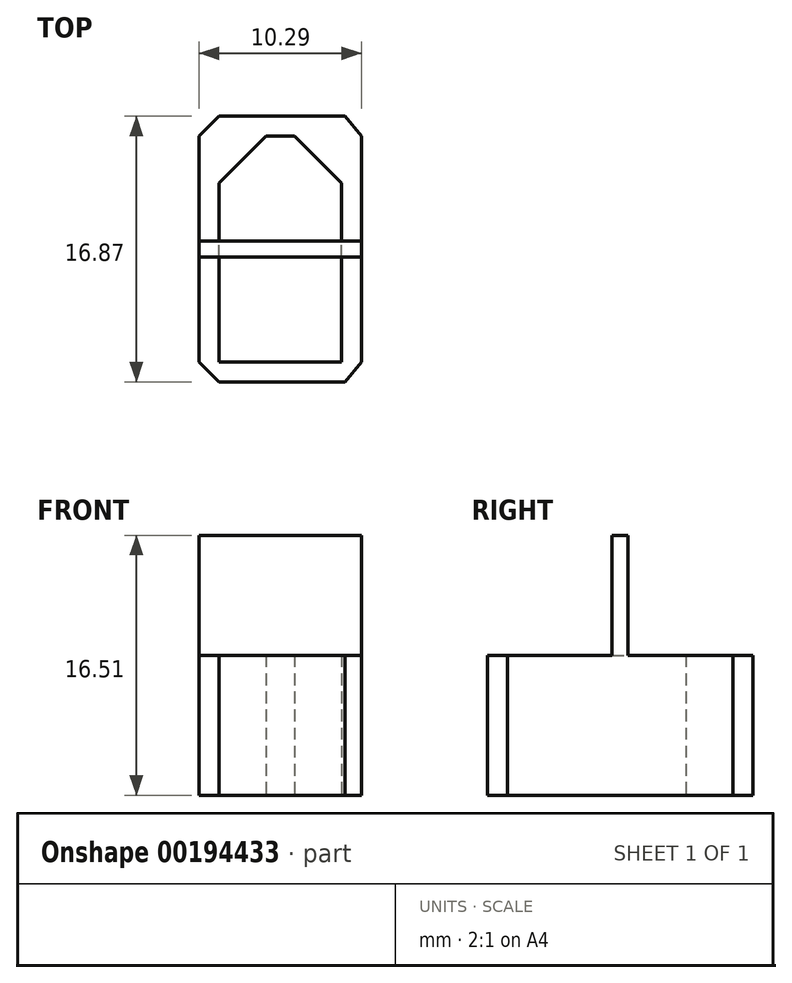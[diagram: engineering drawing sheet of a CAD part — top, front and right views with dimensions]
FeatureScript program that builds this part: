
annotation { "Feature Type Name" : "Feature", "Feature Type Description" : "" }
export const myFeature = defineFeature(function(context is Context, id is Id, definition is map)
    precondition{}
    {
        {
            var Q0;
            Q0=qCreatedBy(makeId("Top.planeOp"),FACE);
            var sketch = newSketch(context, id + "F0", { "sketchPlane" : qUnion([Q0])});
            skLineSegment(sketch, "E0.bottom", {"start": v(0, 0) * mm, "end": v(7.75, 0) * mm});
            skLineSegment(sketch, "E0.top", {"start": v(2.97, 14.33) * mm, "end": v(4.77, 14.33) * mm});
            skLineSegment(sketch, "E0.left", {"start": v(0, 0) * mm, "end": v(0, 11.35) * mm});
            skLineSegment(sketch, "E0.right", {"start": v(7.75, 0) * mm, "end": v(7.75, 11.35) * mm});
            skLineSegment(sketch, "E1", {"start": v(4.77, 14.33) * mm, "end": v(7.75, 11.35) * mm});
            skLineSegment(sketch, "E2", {"start": v(2.97, 14.33) * mm, "end": v(0, 11.35) * mm});
            skLineSegment(sketch, "E3.0", {"start": v(9.02, 0) * mm, "end": v(9.02, 14.33) * mm});
            skLineSegment(sketch, "E4.0", {"start": v(0, 15.6) * mm, "end": v(7.98, 15.6) * mm});
            skLineSegment(sketch, "E5.0", {"start": v(-1.27, 0) * mm, "end": v(-1.27, 14.33) * mm});
            skLineSegment(sketch, "E6.0", {"start": v(0, -1.27) * mm, "end": v(7.98, -1.27) * mm});
            skLineSegment(sketch, "E7", {"start": v(0, 15.6) * mm, "end": v(-1.27, 14.33) * mm});
            skLineSegment(sketch, "E8", {"start": v(7.98, 15.6) * mm, "end": v(9.02, 14.33) * mm});
            skLineSegment(sketch, "E9", {"start": v(9.02, 0) * mm, "end": v(7.98, -1.27) * mm});
            skLineSegment(sketch, "E10", {"start": v(0, -1.27) * mm, "end": v(-1.27, 0) * mm});
            skSolve(sketch);
        }
        {
            var Q0;
            Q0=makeQuery(id+"F0.imprint","IMPRINT",FACE,{"disambiguationData":[TD([[makeQuery(id+"F0.imprint","IMPRINT",EDGE,{"derivedFrom":sQuery(id+"F0.wireOp",EDGE,"E0.bottom")}),-1.0]])]});
            extrude(context, id + "F1", {"entities" : qUnion([Q0]), "depth" : 8.9 * mm});
        }
        {
            var Q0;
            Q0=makeQuery(id+"F1.opExtrude","CAP_FACE",FACE,{"disambiguationData":[OSD([sQuery(id+"F0.wireOp",EDGE,"E0.bottom"),sQuery(id+"F0.wireOp",EDGE,"E0.top"),sQuery(id+"F0.wireOp",EDGE,"E0.left"),sQuery(id+"F0.wireOp",EDGE,"E0.right"),sQuery(id+"F0.wireOp",EDGE,"E1"),sQuery(id+"F0.wireOp",EDGE,"E2"),sQuery(id+"F0.wireOp",EDGE,"E3.0"),sQuery(id+"F0.wireOp",EDGE,"E4.0"),sQuery(id+"F0.wireOp",EDGE,"E5.0"),sQuery(id+"F0.wireOp",EDGE,"E6.0"),sQuery(id+"F0.wireOp",EDGE,"E7"),sQuery(id+"F0.wireOp",EDGE,"E8"),sQuery(id+"F0.wireOp",EDGE,"E9"),sQuery(id+"F0.wireOp",EDGE,"E10")])],"isStart":false});
            var sketch = newSketch(context, id + "F2", { "sketchPlane" : qUnion([Q0])});
            skLineSegment(sketch, "E11.bottom", {"start": v(-1.27, 7.67) * mm, "end": v(9.02, 7.67) * mm});
            skLineSegment(sketch, "E11.top", {"start": v(-1.27, 6.65) * mm, "end": v(9.02, 6.65) * mm});
            skLineSegment(sketch, "E11.left", {"start": v(-1.27, 7.67) * mm, "end": v(-1.27, 6.65) * mm});
            skLineSegment(sketch, "E11.right", {"start": v(9.02, 7.67) * mm, "end": v(9.02, 6.65) * mm});
            skSolve(sketch);
        }
        {
            var Q0;
            {var subQ0=sQuery(id+"F2.wireOp",EDGE,"E11.right");Q0=makeQuery(id+"F2.imprint","IMPRINT",FACE,{"disambiguationData":[TD([[makeQuery(id+"F2.imprint","IMPRINT",EDGE,{"derivedFrom":subQ0}),1.0]])]});}
            var Q1;
            {var subQ0=sQuery(id+"F2.wireOp",EDGE,"E11.bottom");var subQ1=makeQuery(id+"F1.opExtrude","CAP_EDGE",EDGE,{"disambiguationData":[OSD([sQuery(id+"F0.wireOp",EDGE,"E0.left")])],"isStart":false});var subQ2=makeQuery(id+"F2.imprint","INTERSECT",VERTEX,{"derivedFrom":[subQ1,subQ0]});Q1=makeQuery(id+"F2.imprint","IMPRINT",FACE,{"disambiguationData":[TD([[makeQuery(id+"F2.imprint","IMPRINT",EDGE,{"disambiguationData":[TD([[subQ2,-1.0]])],"derivedFrom":subQ0}),-1.0]])]});}
            var Q2;
            {var subQ0=sQuery(id+"F2.wireOp",EDGE,"E11.left");Q2=makeQuery(id+"F2.imprint","IMPRINT",FACE,{"disambiguationData":[TD([[makeQuery(id+"F2.imprint","IMPRINT",EDGE,{"derivedFrom":subQ0}),-1.0]])]});}
            extrude(context, id + "F3", {"entities" : qUnion([Q0, Q1, Q2]), "operationType" : NewBodyOperationType.ADD, "depth" : 7.62 * mm});
        }
    });
